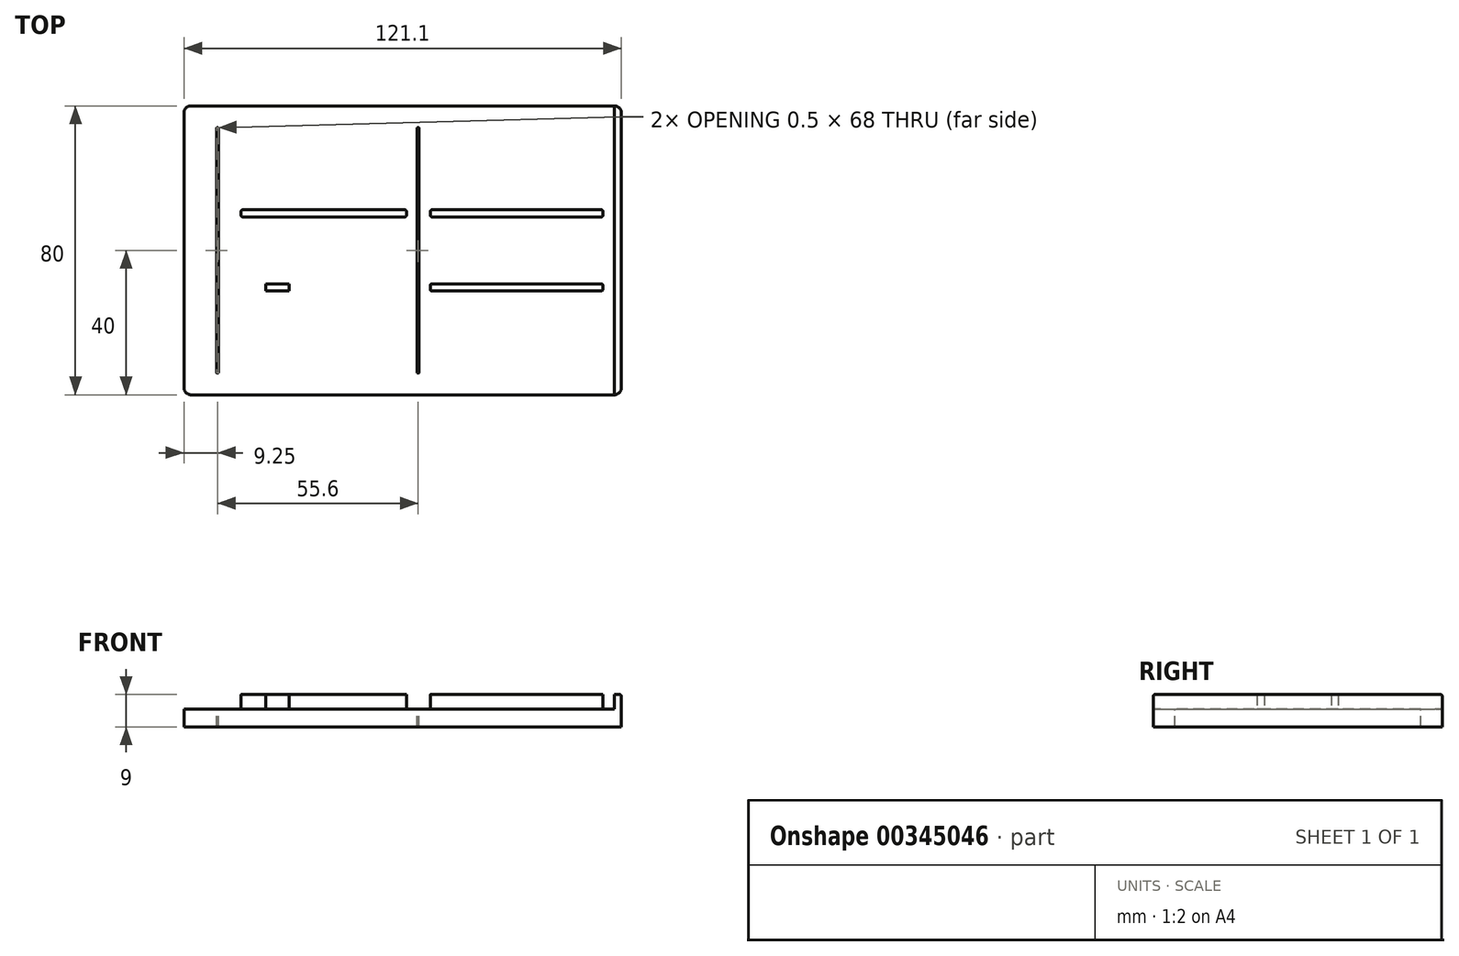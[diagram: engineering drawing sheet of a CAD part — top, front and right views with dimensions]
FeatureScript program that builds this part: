
annotation { "Feature Type Name" : "Feature", "Feature Type Description" : "" }
export const myFeature = defineFeature(function(context is Context, id is Id, definition is map)
    precondition{}
    {
        {
            var Q0;
            Q0=qCreatedBy(makeId("Top.planeOp"),FACE);
            var sketch = newSketch(context, id + "F0", { "sketchPlane" : qUnion([Q0])});
            skLineSegment(sketch, "E0.bottom", {"start": v(0, 0) * mm, "end": v(119.1, 0) * mm});
            skLineSegment(sketch, "E0.top", {"start": v(0, 80) * mm, "end": v(119.1, 80) * mm});
            skLineSegment(sketch, "E0.left", {"start": v(0, 0) * mm, "end": v(0, 80) * mm});
            skLineSegment(sketch, "E0.right", {"start": v(119.1, 0) * mm, "end": v(119.1, 80) * mm});
            skSolve(sketch);
        }
        {
            var Q0;
            Q0 = qSketchRegion(id + "F0", true);
            extrude(context, id + "F1", {"entities" : qUnion([Q0]), "depth" : 5 * mm});
        }
        {
            var Q0;
            Q0=makeQuery(id+"F1.opExtrude","CAP_FACE",FACE,{"disambiguationData":[OSD([sQuery(id+"F0.wireOp",EDGE,"E0.bottom"),sQuery(id+"F0.wireOp",EDGE,"E0.top"),sQuery(id+"F0.wireOp",EDGE,"E0.left"),sQuery(id+"F0.wireOp",EDGE,"E0.right")])],"isStart":false});
            var sketch = newSketch(context, id + "F2", { "sketchPlane" : qUnion([Q0])});
            skLineSegment(sketch, "E1", {"start": v(64.6, 25) * mm, "end": v(64.6, 74) * mm});
            skLineSegment(sketch, "E2", {"start": v(64.6, 25) * mm, "end": v(64.6, 6) * mm});
            skLineSegment(sketch, "E3", {"start": v(64.6, 74) * mm, "end": v(65.1, 74) * mm});
            skLineSegment(sketch, "E4", {"start": v(65.1, 74) * mm, "end": v(65.1, 6) * mm});
            skLineSegment(sketch, "E5", {"start": v(65.1, 6) * mm, "end": v(64.6, 6) * mm});
            skSolve(sketch);
        }
        {
            var Q0;
            Q0 = qSketchRegion(id + "F2", true);
            extrude(context, id + "F3", {"entities" : qUnion([Q0]), "operationType" : NewBodyOperationType.REMOVE, "oppositeDirection" : true, "depth" : 63.1 * mm});
        }
        {
            var Q0;
            Q0=makeQuery(id+"F1.opExtrude","CAP_FACE",FACE,{"disambiguationData":[OSD([sQuery(id+"F0.wireOp",EDGE,"E0.bottom"),sQuery(id+"F0.wireOp",EDGE,"E0.top"),sQuery(id+"F0.wireOp",EDGE,"E0.left"),sQuery(id+"F0.wireOp",EDGE,"E0.right")])],"isStart":false});
            var sketch = newSketch(context, id + "F4", { "sketchPlane" : qUnion([Q0])});
            skLineSegment(sketch, "E6", {"start": v(39.12, 49.25) * mm, "end": v(61.6, 49.25) * mm});
            skLineSegment(sketch, "E7", {"start": v(39.12, 49.25) * mm, "end": v(39.12, 30.75) * mm});
            skPoint(sketch, "E7.endSnap0", {"position": v(39.12, 40) * mm});
            skLineSegment(sketch, "E8", {"start": v(39.12, 49.25) * mm, "end": v(15.8, 49.25) * mm});
            skLineSegment(sketch, "E9", {"start": v(15.8, 30.75) * mm, "end": v(61.6, 30.75) * mm});
            skLineSegment(sketch, "E10.bottom", {"start": v(15.8, 49.25) * mm, "end": v(61.6, 49.25) * mm});
            skLineSegment(sketch, "E10.top", {"start": v(15.8, 51.25) * mm, "end": v(61.6, 51.25) * mm});
            skLineSegment(sketch, "E10.left", {"start": v(15.8, 49.25) * mm, "end": v(15.8, 51.25) * mm});
            skLineSegment(sketch, "E10.right", {"start": v(61.6, 49.25) * mm, "end": v(61.6, 51.25) * mm});
            skLineSegment(sketch, "E11.top", {"start": v(15.8, 28.75) * mm, "end": v(61.6, 28.75) * mm});
            skLineSegment(sketch, "E11.left", {"start": v(15.8, 30.75) * mm, "end": v(15.8, 28.75) * mm});
            skLineSegment(sketch, "E11.right", {"start": v(61.6, 30.75) * mm, "end": v(61.6, 28.75) * mm});
            skLineSegment(sketch, "E12.bottom", {"start": v(39.12, 30.75) * mm, "end": v(48.1, 30.75) * mm});
            skLineSegment(sketch, "E12.top", {"start": v(39.8, 28.75) * mm, "end": v(48.1, 28.75) * mm});
            skLineSegment(sketch, "E12.right", {"start": v(48.1, 30.75) * mm, "end": v(48.1, 28.75) * mm});
            skLineSegment(sketch, "E13.bottom", {"start": v(54.6, 30.75) * mm, "end": v(61.6, 30.75) * mm});
            skLineSegment(sketch, "E13.top", {"start": v(54.6, 28.75) * mm, "end": v(61.6, 28.75) * mm});
            skLineSegment(sketch, "E13.left", {"start": v(54.6, 30.75) * mm, "end": v(54.6, 28.75) * mm});
            skLineSegment(sketch, "E14.bottom", {"start": v(15.8, 30.75) * mm, "end": v(22.6, 30.75) * mm});
            skLineSegment(sketch, "E14.top", {"start": v(15.8, 28.75) * mm, "end": v(22.6, 28.75) * mm});
            skLineSegment(sketch, "E14.right", {"start": v(22.6, 30.75) * mm, "end": v(22.6, 28.75) * mm});
            skLineSegment(sketch, "E15.bottom", {"start": v(29.1, 30.75) * mm, "end": v(35.9, 30.75) * mm});
            skLineSegment(sketch, "E15.top", {"start": v(29.1, 28.75) * mm, "end": v(35.9, 28.75) * mm});
            skLineSegment(sketch, "E15.left", {"start": v(29.1, 30.75) * mm, "end": v(29.1, 28.75) * mm});
            skLineSegment(sketch, "E15.right", {"start": v(35.9, 30.75) * mm, "end": v(35.9, 28.75) * mm});
            skLineSegment(sketch, "E16", {"start": v(48.1, 30.75) * mm, "end": v(41.1, 30.75) * mm});
            skLineSegment(sketch, "E17", {"start": v(41.1, 28.75) * mm, "end": v(41.1, 30.75) * mm});
            skLineSegment(sketch, "E18", {"start": v(22.6, 49.25) * mm, "end": v(22.6, 51.25) * mm});
            skLineSegment(sketch, "E19", {"start": v(29.1, 49.25) * mm, "end": v(29.1, 51.25) * mm});
            skLineSegment(sketch, "E20", {"start": v(35.9, 28.75) * mm, "end": v(35.9, 30.75) * mm});
            skLineSegment(sketch, "E21", {"start": v(48.1, 28.75) * mm, "end": v(48.1, 30.75) * mm});
            skLineSegment(sketch, "E22", {"start": v(54.6, 28.75) * mm, "end": v(54.6, 30.75) * mm});
            skLineSegment(sketch, "E23.trimOffspring", {"start": v(35.9, 49.25) * mm, "end": v(35.9, 51.25) * mm});
            skLineSegment(sketch, "E24.trimOffspring", {"start": v(41.1, 49.25) * mm, "end": v(41.1, 51.25) * mm});
            skLineSegment(sketch, "E25.trimOffspring", {"start": v(48.1, 49.25) * mm, "end": v(48.1, 51.25) * mm});
            skLineSegment(sketch, "E26.trimOffspring", {"start": v(54.6, 49.25) * mm, "end": v(54.6, 51.25) * mm});
            skLineSegment(sketch, "E27", {"start": v(39.12, 40) * mm, "end": v(39.12, 30.75) * mm});
            skSolve(sketch);
        }
        {
            var Q0;
            {var subQ0=sQuery(id+"F4.wireOp",EDGE,"E19");Q0=makeQuery(id+"F4.imprint","IMPRINT",FACE,{"disambiguationData":[TD([[makeQuery(id+"F4.imprint","IMPRINT",EDGE,{"derivedFrom":subQ0}),-1.0]])]});}
            var Q1;
            {var subQ0=sQuery(id+"F4.wireOp",EDGE,"E23.trimOffspring");Q1=makeQuery(id+"F4.imprint","IMPRINT",FACE,{"disambiguationData":[TD([[makeQuery(id+"F4.imprint","IMPRINT",EDGE,{"derivedFrom":subQ0}),-1.0]])]});}
            var Q2;
            {var subQ0=sQuery(id+"F4.wireOp",EDGE,"E24.trimOffspring");Q2=makeQuery(id+"F4.imprint","IMPRINT",FACE,{"disambiguationData":[TD([[makeQuery(id+"F4.imprint","IMPRINT",EDGE,{"derivedFrom":subQ0}),-1.0]])]});}
            var Q3;
            {var subQ0=sQuery(id+"F4.wireOp",EDGE,"E25.trimOffspring");Q3=makeQuery(id+"F4.imprint","IMPRINT",FACE,{"disambiguationData":[TD([[makeQuery(id+"F4.imprint","IMPRINT",EDGE,{"derivedFrom":subQ0}),-1.0]])]});}
            var Q4;
            {var subQ0=sQuery(id+"F4.wireOp",EDGE,"E10.left");Q4=makeQuery(id+"F4.imprint","IMPRINT",FACE,{"disambiguationData":[TD([[makeQuery(id+"F4.imprint","IMPRINT",EDGE,{"derivedFrom":subQ0}),-1.0]])]});}
            var Q5;
            {var subQ0=sQuery(id+"F4.wireOp",EDGE,"E18");Q5=makeQuery(id+"F4.imprint","IMPRINT",FACE,{"disambiguationData":[TD([[makeQuery(id+"F4.imprint","IMPRINT",EDGE,{"derivedFrom":subQ0}),-1.0]])]});}
            var Q6;
            {var subQ0=sQuery(id+"F4.wireOp",EDGE,"E10.right");Q6=makeQuery(id+"F4.imprint","IMPRINT",FACE,{"disambiguationData":[TD([[makeQuery(id+"F4.imprint","IMPRINT",EDGE,{"derivedFrom":subQ0}),1.0]])]});}
            var Q7;
            Q7=makeQuery(id+"F4.imprint","IMPRINT",FACE,{"disambiguationData":[TD([[makeQuery(id+"F4.imprint","IMPRINT",EDGE,{"derivedFrom":sQuery(id+"F4.wireOp",EDGE,"E16")}),1.0]])]});
            var Q8;
            Q8=makeQuery(id+"F4.imprint","IMPRINT",FACE,{"disambiguationData":[TD([[makeQuery(id+"F4.imprint","IMPRINT",EDGE,{"derivedFrom":sQuery(id+"F4.wireOp",EDGE,"E15.bottom")}),-1.0]])]});
            var Q9;
            Q9=makeQuery(id+"F4.imprint","IMPRINT",FACE,{"disambiguationData":[TD([[makeQuery(id+"F4.imprint","IMPRINT",EDGE,{"derivedFrom":sQuery(id+"F4.wireOp",EDGE,"E13.bottom")}),-1.0]])]});
            var Q10;
            {var subQ5=sQuery(id+"F4.wireOp",EDGE,"E12.bottom");Q10=makeQuery(id+"F4.imprint","IMPRINT",FACE,{"disambiguationData":[TD([[makeQuery(id+"F4.imprint","IMPRINT",EDGE,{"derivedFrom":subQ5}),-1.0]])]});}
            var Q11;
            {var subQ2=sQuery(id+"F4.wireOp",EDGE,"E21");Q11=makeQuery(id+"F4.imprint","IMPRINT",FACE,{"disambiguationData":[TD([[makeQuery(id+"F4.imprint","IMPRINT",EDGE,{"derivedFrom":subQ2}),-1.0]])]});}
            var Q12;
            {var subQ0=sQuery(id+"F4.wireOp",EDGE,"E14.right");Q12=makeQuery(id+"F4.imprint","IMPRINT",FACE,{"disambiguationData":[TD([[makeQuery(id+"F4.imprint","IMPRINT",EDGE,{"derivedFrom":subQ0}),1.0]])]});}
            var Q13;
            Q13=makeQuery(id+"F4.imprint","IMPRINT",FACE,{"disambiguationData":[TD([[makeQuery(id+"F4.imprint","IMPRINT",EDGE,{"derivedFrom":sQuery(id+"F4.wireOp",EDGE,"E14.bottom")}),-1.0]])]});
            extrude(context, id + "F5", {"entities" : qUnion([Q0, Q1, Q2, Q3, Q4, Q5, Q6, Q7, Q8, Q9, Q10, Q11, Q12, Q13]), "operationType" : NewBodyOperationType.ADD, "depth" : 4 * mm});
        }
        {
            var Q0;
            Q0=makeQuery(id+"F1.opExtrude","CAP_FACE",FACE,{"disambiguationData":[OSD([sQuery(id+"F0.wireOp",EDGE,"E0.bottom"),sQuery(id+"F0.wireOp",EDGE,"E0.top"),sQuery(id+"F0.wireOp",EDGE,"E0.left"),sQuery(id+"F0.wireOp",EDGE,"E0.right")])],"isStart":false});
            var sketch = newSketch(context, id + "F6", { "sketchPlane" : qUnion([Q0])});
            skLineSegment(sketch, "E28", {"start": v(68.2, 51.25) * mm, "end": v(116, 51.25) * mm});
            skLineSegment(sketch, "E29", {"start": v(116, 51.25) * mm, "end": v(116, 49.25) * mm});
            skLineSegment(sketch, "E30", {"start": v(116, 49.25) * mm, "end": v(68.2, 49.25) * mm});
            skLineSegment(sketch, "E31", {"start": v(68.2, 49.25) * mm, "end": v(68.2, 51.25) * mm});
            skLineSegment(sketch, "E32", {"start": v(68.2, 30.75) * mm, "end": v(68.2, 28.75) * mm});
            skLineSegment(sketch, "E33", {"start": v(68.2, 28.75) * mm, "end": v(116, 28.75) * mm});
            skLineSegment(sketch, "E34", {"start": v(116, 28.75) * mm, "end": v(116, 30.75) * mm});
            skLineSegment(sketch, "E35", {"start": v(116, 30.75) * mm, "end": v(68.2, 30.75) * mm});
            skSolve(sketch);
        }
        {
            var Q0;
            Q0=makeQuery(id+"F6.imprint","IMPRINT",FACE,{"disambiguationData":[TD([[makeQuery(id+"F6.imprint","IMPRINT",EDGE,{"derivedFrom":sQuery(id+"F6.wireOp",EDGE,"E28")}),-1.0]])]});
            var Q1;
            Q1=makeQuery(id+"F6.imprint","IMPRINT",FACE,{"disambiguationData":[TD([[makeQuery(id+"F6.imprint","IMPRINT",EDGE,{"derivedFrom":sQuery(id+"F6.wireOp",EDGE,"E32")}),1.0]])]});
            extrude(context, id + "F7", {"entities" : qUnion([Q0, Q1]), "operationType" : NewBodyOperationType.ADD, "depth" : 4 * mm});
        }
        {
            var Q0;
            Q0=makeQuery(id+"F1.opExtrude","CAP_FACE",FACE,{"disambiguationData":[OSD([sQuery(id+"F0.wireOp",EDGE,"E0.bottom"),sQuery(id+"F0.wireOp",EDGE,"E0.top"),sQuery(id+"F0.wireOp",EDGE,"E0.left"),sQuery(id+"F0.wireOp",EDGE,"E0.right")])],"isStart":false});
            var sketch = newSketch(context, id + "F8", { "sketchPlane" : qUnion([Q0])});
            skLineSegment(sketch, "E36.bottom", {"start": v(9, 74) * mm, "end": v(9.5, 74) * mm});
            skLineSegment(sketch, "E36.top", {"start": v(9, 6) * mm, "end": v(9.5, 6) * mm});
            skLineSegment(sketch, "E36.left", {"start": v(9, 74) * mm, "end": v(9, 6) * mm});
            skLineSegment(sketch, "E36.right", {"start": v(9.5, 74) * mm, "end": v(9.5, 6) * mm});
            skSolve(sketch);
        }
        {
            var Q0;
            Q0=makeQuery(id+"F8.imprint","IMPRINT",FACE,{"disambiguationData":[TD([[makeQuery(id+"F8.imprint","IMPRINT",EDGE,{"derivedFrom":sQuery(id+"F8.wireOp",EDGE,"E36.bottom")}),-1.0]])]});
            extrude(context, id + "F9", {"entities" : qUnion([Q0]), "operationType" : NewBodyOperationType.REMOVE, "oppositeDirection" : true, "depth" : 25 * mm});
        }
        {
            var Q0;
            Q0=makeQuery(id+"F1.opExtrude","SWEPT_FACE",FACE,{"disambiguationData":[OSD([sQuery(id+"F0.wireOp",EDGE,"E0.right")])]});
            var sketch = newSketch(context, id + "F10", { "sketchPlane" : qUnion([Q0])});
            skLineSegment(sketch, "E37.bottom", {"start": v(0, 5) * mm, "end": v(80, 5) * mm});
            skLineSegment(sketch, "E37.top", {"start": v(0, 0) * mm, "end": v(80, 0) * mm});
            skLineSegment(sketch, "E37.left", {"start": v(0, 5) * mm, "end": v(0, 0) * mm});
            skLineSegment(sketch, "E37.right", {"start": v(80, 5) * mm, "end": v(80, 0) * mm});
            skSolve(sketch);
        }
        {
            var Q0;
            Q0 = qSketchRegion(id + "F10", true);
            extrude(context, id + "F11", {"entities" : qUnion([Q0]), "operationType" : NewBodyOperationType.ADD, "depth" : 2 * mm});
        }
        {
            var Q0;
            Q0=makeQuery(id+"F11.boolean.opBoolean","MERGE",FACE,{"derivedFrom":[makeQuery(id+"F1.opExtrude","CAP_FACE",FACE,{"disambiguationData":[OSD([sQuery(id+"F0.wireOp",EDGE,"E0.bottom"),sQuery(id+"F0.wireOp",EDGE,"E0.top"),sQuery(id+"F0.wireOp",EDGE,"E0.left"),sQuery(id+"F0.wireOp",EDGE,"E0.right")])],"isStart":false}),makeQuery(id+"F11.opExtrude","SWEPT_FACE",FACE,{"disambiguationData":[OSD([sQuery(id+"F10.wireOp",EDGE,"E37.bottom")])]})]});
            var sketch = newSketch(context, id + "F12", { "sketchPlane" : qUnion([Q0])});
            skLineSegment(sketch, "E38", {"start": v(121.1, 47.44) * mm, "end": v(119.1, 47.44) * mm});
            skLineSegment(sketch, "E39", {"start": v(119.1, 47.44) * mm, "end": v(119.1, 80) * mm});
            skLineSegment(sketch, "E40", {"start": v(119.1, 80) * mm, "end": v(119.1, 0) * mm});
            skLineSegment(sketch, "E41", {"start": v(119.1, 0) * mm, "end": v(121.1, 0) * mm});
            skLineSegment(sketch, "E42", {"start": v(121.1, 0) * mm, "end": v(121.1, 80) * mm});
            skLineSegment(sketch, "E43", {"start": v(121.1, 80) * mm, "end": v(119.1, 80) * mm});
            skSolve(sketch);
        }
        {
            var Q0;
            {var subQ0=sQuery(id+"F12.wireOp",EDGE,"E38");Q0=makeQuery(id+"F12.imprint","IMPRINT",FACE,{"disambiguationData":[TD([[makeQuery(id+"F12.imprint","IMPRINT",EDGE,{"derivedFrom":subQ0}),-1.0]])]});}
            var Q1;
            {var subQ0=sQuery(id+"F12.wireOp",EDGE,"E38");Q1=makeQuery(id+"F12.imprint","IMPRINT",FACE,{"disambiguationData":[TD([[makeQuery(id+"F12.imprint","IMPRINT",EDGE,{"derivedFrom":subQ0}),1.0]])]});}
            extrude(context, id + "F13", {"entities" : qUnion([Q0, Q1]), "operationType" : NewBodyOperationType.ADD, "depth" : 4 * mm});
        }
        {
            var Q0;
            Q0=makeQuery(id+"F1.opExtrude","SWEPT_EDGE",EDGE,{"disambiguationData":[OSD([sQuery(id+"F0.wireOp",EDGE,"E0.top"),sQuery(id+"F0.wireOp",EDGE,"E0.left")])]});
            var Q1;
            Q1=makeQuery(id+"F1.opExtrude","SWEPT_EDGE",EDGE,{"disambiguationData":[OSD([sQuery(id+"F0.wireOp",EDGE,"E0.bottom"),sQuery(id+"F0.wireOp",EDGE,"E0.left")])]});
            var Q2;
            Q2=makeQuery(id+"F13.boolean.opBoolean","MERGE",EDGE,{"derivedFrom":[makeQuery(id+"F11.opExtrude","CAP_EDGE",EDGE,{"disambiguationData":[OSD([sQuery(id+"F10.wireOp",EDGE,"E37.right")])],"isStart":false}),makeQuery(id+"F13.opExtrude","SWEPT_EDGE",EDGE,{"disambiguationData":[OSD([sQuery(id+"F12.wireOp",EDGE,"E42"),sQuery(id+"F12.wireOp",EDGE,"E43")])]})]});
            var Q3;
            Q3=makeQuery(id+"F13.boolean.opBoolean","MERGE",EDGE,{"derivedFrom":[makeQuery(id+"F11.opExtrude","CAP_EDGE",EDGE,{"disambiguationData":[OSD([sQuery(id+"F10.wireOp",EDGE,"E37.left")])],"isStart":false}),makeQuery(id+"F13.opExtrude","SWEPT_EDGE",EDGE,{"disambiguationData":[OSD([sQuery(id+"F12.wireOp",EDGE,"E41"),sQuery(id+"F12.wireOp",EDGE,"E42")])]})]});
            fillet(context, id + "F14", {"entities" : qUnion([Q0, Q1, Q2, Q3]), "radius" : 2 * mm, "tangentPropagation" : true, "allowEdgeOverflow" : false});
        }
        {
            var Q0;
            Q0=makeQuery(id+"F5.opExtrude","SWEPT_EDGE",EDGE,{"disambiguationData":[OSD([sQuery(id+"F4.wireOp",EDGE,"E10.bottom"),sQuery(id+"F4.wireOp",EDGE,"E10.left")])]});
            var Q1;
            Q1=makeQuery(id+"F5.opExtrude","SWEPT_EDGE",EDGE,{"disambiguationData":[OSD([sQuery(id+"F4.wireOp",EDGE,"E10.top"),sQuery(id+"F4.wireOp",EDGE,"E10.left")])]});
            var Q2;
            Q2=makeQuery(id+"F5.opExtrude","SWEPT_EDGE",EDGE,{"disambiguationData":[OSD([sQuery(id+"F4.wireOp",EDGE,"E10.bottom"),sQuery(id+"F4.wireOp",EDGE,"E10.right")])]});
            var Q3;
            Q3=makeQuery(id+"F5.opExtrude","SWEPT_EDGE",EDGE,{"disambiguationData":[OSD([sQuery(id+"F4.wireOp",EDGE,"E10.top"),sQuery(id+"F4.wireOp",EDGE,"E10.right")])]});
            var Q4;
            Q4=makeQuery(id+"F7.opExtrude","SWEPT_EDGE",EDGE,{"disambiguationData":[OSD([sQuery(id+"F6.wireOp",EDGE,"E30"),sQuery(id+"F6.wireOp",EDGE,"E31")])]});
            var Q5;
            Q5=makeQuery(id+"F7.opExtrude","SWEPT_EDGE",EDGE,{"disambiguationData":[OSD([sQuery(id+"F6.wireOp",EDGE,"E28"),sQuery(id+"F6.wireOp",EDGE,"E31")])]});
            var Q6;
            Q6=makeQuery(id+"F7.opExtrude","SWEPT_EDGE",EDGE,{"disambiguationData":[OSD([sQuery(id+"F6.wireOp",EDGE,"E29"),sQuery(id+"F6.wireOp",EDGE,"E30")])]});
            var Q7;
            Q7=makeQuery(id+"F7.opExtrude","SWEPT_EDGE",EDGE,{"disambiguationData":[OSD([sQuery(id+"F6.wireOp",EDGE,"E28"),sQuery(id+"F6.wireOp",EDGE,"E29")])]});
            var Q8;
            Q8=makeQuery(id+"F7.opExtrude","SWEPT_EDGE",EDGE,{"disambiguationData":[OSD([sQuery(id+"F6.wireOp",EDGE,"E33"),sQuery(id+"F6.wireOp",EDGE,"E34")])]});
            var Q9;
            Q9=makeQuery(id+"F7.opExtrude","SWEPT_EDGE",EDGE,{"disambiguationData":[OSD([sQuery(id+"F6.wireOp",EDGE,"E34"),sQuery(id+"F6.wireOp",EDGE,"E35")])]});
            var Q10;
            Q10=makeQuery(id+"F7.opExtrude","SWEPT_EDGE",EDGE,{"disambiguationData":[OSD([sQuery(id+"F6.wireOp",EDGE,"E32"),sQuery(id+"F6.wireOp",EDGE,"E33")])]});
            var Q11;
            Q11=makeQuery(id+"F7.opExtrude","SWEPT_EDGE",EDGE,{"disambiguationData":[OSD([sQuery(id+"F6.wireOp",EDGE,"E32"),sQuery(id+"F6.wireOp",EDGE,"E35")])]});
            var Q12;
            Q12=makeQuery(id+"F5.opExtrude","SWEPT_EDGE",EDGE,{"disambiguationData":[OSD([sQuery(id+"F4.wireOp",EDGE,"E13.top"),sQuery(id+"F4.wireOp",EDGE,"E11.right")])]});
            var Q13;
            Q13=makeQuery(id+"F5.opExtrude","SWEPT_EDGE",EDGE,{"disambiguationData":[OSD([sQuery(id+"F4.wireOp",EDGE,"E13.bottom"),sQuery(id+"F4.wireOp",EDGE,"E11.right")])]});
            var Q14;
            Q14=makeQuery(id+"F5.opExtrude","SWEPT_EDGE",EDGE,{"disambiguationData":[OSD([sQuery(id+"F4.wireOp",EDGE,"E14.top"),sQuery(id+"F4.wireOp",EDGE,"E11.left")])]});
            var Q15;
            Q15=makeQuery(id+"F5.opExtrude","SWEPT_EDGE",EDGE,{"disambiguationData":[OSD([sQuery(id+"F4.wireOp",EDGE,"E14.bottom"),sQuery(id+"F4.wireOp",EDGE,"E11.left")])]});
            fillet(context, id + "F15", {"entities" : qUnion([Q0, Q1, Q2, Q3, Q4, Q5, Q6, Q7, Q8, Q9, Q10, Q11, Q12, Q13, Q14, Q15]), "radius" : .5 * mm, "tangentPropagation" : true, "allowEdgeOverflow" : false});
        }
        {
            var Q0;
            Q0=makeQuery(id+"F9.boolean.opBoolean","COPY",EDGE,{"derivedFrom":makeQuery(id+"F9.opExtrude","SWEPT_EDGE",EDGE,{"disambiguationData":[OSD([sQuery(id+"F8.wireOp",EDGE,"E36.top"),sQuery(id+"F8.wireOp",EDGE,"E36.right")])]})});
            var Q1;
            Q1=makeQuery(id+"F9.boolean.opBoolean","COPY",EDGE,{"derivedFrom":makeQuery(id+"F9.opExtrude","SWEPT_EDGE",EDGE,{"disambiguationData":[OSD([sQuery(id+"F8.wireOp",EDGE,"E36.top"),sQuery(id+"F8.wireOp",EDGE,"E36.left")])]})});
            var Q2;
            Q2=makeQuery(id+"F9.boolean.opBoolean","COPY",EDGE,{"derivedFrom":makeQuery(id+"F9.opExtrude","SWEPT_EDGE",EDGE,{"disambiguationData":[OSD([sQuery(id+"F8.wireOp",EDGE,"E36.bottom"),sQuery(id+"F8.wireOp",EDGE,"E36.right")])]})});
            var Q3;
            Q3=makeQuery(id+"F9.boolean.opBoolean","COPY",EDGE,{"derivedFrom":makeQuery(id+"F9.opExtrude","SWEPT_EDGE",EDGE,{"disambiguationData":[OSD([sQuery(id+"F8.wireOp",EDGE,"E36.bottom"),sQuery(id+"F8.wireOp",EDGE,"E36.left")])]})});
            var Q4;
            Q4=makeQuery(id+"F3.boolean.opBoolean","COPY",EDGE,{"derivedFrom":makeQuery(id+"F3.opExtrude","SWEPT_EDGE",EDGE,{"disambiguationData":[OSD([sQuery(id+"F2.wireOp",EDGE,"E1"),sQuery(id+"F2.wireOp",EDGE,"E3")])]})});
            var Q5;
            Q5=makeQuery(id+"F3.boolean.opBoolean","COPY",EDGE,{"derivedFrom":makeQuery(id+"F3.opExtrude","SWEPT_EDGE",EDGE,{"disambiguationData":[OSD([sQuery(id+"F2.wireOp",EDGE,"E3"),sQuery(id+"F2.wireOp",EDGE,"E4")])]})});
            var Q6;
            Q6=makeQuery(id+"F3.boolean.opBoolean","COPY",EDGE,{"derivedFrom":makeQuery(id+"F3.opExtrude","SWEPT_EDGE",EDGE,{"disambiguationData":[OSD([sQuery(id+"F2.wireOp",EDGE,"E2"),sQuery(id+"F2.wireOp",EDGE,"E5")])]})});
            var Q7;
            Q7=makeQuery(id+"F3.boolean.opBoolean","COPY",EDGE,{"derivedFrom":makeQuery(id+"F3.opExtrude","SWEPT_EDGE",EDGE,{"disambiguationData":[OSD([sQuery(id+"F2.wireOp",EDGE,"E4"),sQuery(id+"F2.wireOp",EDGE,"E5")])]})});
            fillet(context, id + "F16", {"entities" : qUnion([Q0, Q1, Q2, Q3, Q4, Q5, Q6, Q7]), "radius" : .1 * mm, "tangentPropagation" : true, "allowEdgeOverflow" : false});
        }
        {
            var Q0;
            Q0=makeQuery(id+"F13.opExtrude","CAP_EDGE",EDGE,{"disambiguationData":[OSD([sQuery(id+"F12.wireOp",EDGE,"E42")])],"isStart":false});
            fillet(context, id + "F17", {"entities" : qUnion([Q0]), "radius" : .5 * mm, "tangentPropagation" : true, "allowEdgeOverflow" : false});
        }
    });
